# Revit family: Gira_5374005
name_source: partatom
category: Electrical Fixtures
revit_build: Autodesk Revit 2017 (Build: 20160225_1515(x64)
units: mm (PartAtom-declared; Revit-internal decimal feet)

## family parameters
Cut with Voids When Loaded = No
Host = Face
Maintain Annotation Orientation = Yes
Part Type = Normal
Room Calculation Point = No
Round Connector Dimension = Use Diameter
Shared = No

## types (1)
- S3000 Beweg.m.aufs. 1,10 m Komfort BT System 55 Schwarz m
    Abdimmfunktion mit Dimmeinsatz = No
    Ansprechempfindlichkeit einstellbar = Yes
    Ansprechhelligkeit einstellbar = No
    Ausführung = Bewegungsmelder
    Available = Yes
    Category = Bewegungsmelder-Sensor
    Data sheet (1) = https://katalog.gira.de
    Default Elevation = 1219 mm
    Erfassungswinkel horizontal = 1 - 180
    Farbe = schwarz
    GTIN = 4010337049531
    Geeignet für Schutzart (IP) = IP20
    Geeignet für drahtlose Übertragung = No
    HAN = 5374005
    HLK-Ansteuerung = No
    Halogenfrei = No
    HeinzeBIM = https://bimportal.heinze.de
    Keynote = Bewegungsmelder_1,10m
    Konstantlichtregelung = No
    Manufacturer URL = https://www.gira.de
    Max. Einschaltdauer = 1800 s
    Max. Reichweite frontal = 10 m
    Max. Reichweite zu einer Seite = 6 m
    Min. Einschaltdauer = 10 s
    Montageart = unter Putz
    Montagehöhe = 1,1 m
    Name = S3000 Beweg.m.aufs. 1,10 m Komfort BT System 55 Schwarz m
    Region = DE
    Teach-Funktion für Ansprechhelligkeit = No
    Tierschneise = Yes
    Treppenhausüberwachung = Yes
    URL = http://katalog.gira.de
    Unterkriechschutz/Rückfeldüberwachung = No
    Vernetzbar = Yes
    Werkstoff = sonstige
    Werkstoffgüte = sonstige

## geometry (parser evidence)
native form markers: Blend x2, Sweep x3
no freeform markers — native parametric forms only
